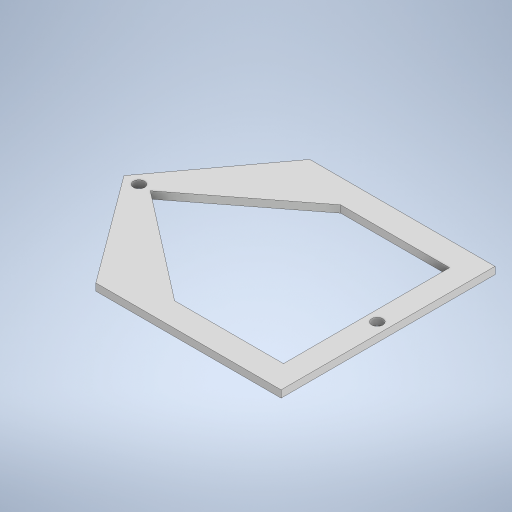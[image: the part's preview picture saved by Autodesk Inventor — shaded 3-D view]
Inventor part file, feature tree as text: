
AUTODESK INVENTOR PART (.ipt)
format: ipt  version: 2024 (Build 280153000, 153)  size: 302,080 bytes
history: native  units: in
note: dims shown in document units (in); Inventor stores cm internally (conversion verified against a paired STEP export)
features: extrude x2, plane x1
ambient origin geometry x8: Origin, YZ Plane, XZ Plane, XY Plane, X Axis, Y Axis, Z Axis, Center Point
bodies: Solid1 (feature_tree)
feature tree (3):
  plane  "Work Plane4"
  extrude  "Extrusion3"  Depth=3.2874in
  extrude  "Extrusion5"  Depth=0.1181in
